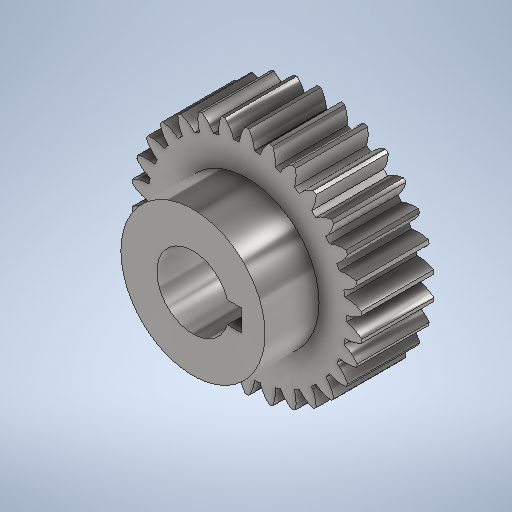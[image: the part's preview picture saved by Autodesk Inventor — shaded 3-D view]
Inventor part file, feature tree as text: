
AUTODESK INVENTOR PART (.ipt)
format: ipt  version: 2025.2 (Build 292293000, 293)  size: 447,488 bytes
history: native  units: in
note: dims shown in document units (in); Inventor stores cm internally (conversion verified against a paired STEP export)
features: sketch x5, extrude x5, fillet x1, pattern_circular x1
ambient origin geometry x8: Origin, YZ Plane, XZ Plane, XY Plane, X Axis, Y Axis, Z Axis, Center Point
bodies: Solid1 (feature_tree)
feature tree (12):
  sketch  "Sketch1"  dims[d0=2.5197in d1=2.3622in]
  extrude  "Extrusion1"  Depth=2.3622in
  extrude  "Extrusion2"  Depth=0.1236in
  fillet  "Fillet1"  Radius=0.0394in
  pattern_circular  "Circular Pattern1"  Count=2  [1 undecoded]
  extrude  "Extrusion3"  Depth=0.0039in
  sketch  "Sketch3"  dims[d5=0.1654in d6=0.7874in d7=0.0in]
  extrude  "Extrusion4"  Depth=0.2362in
  extrude  "Extrusion5"  Depth=0.7874in
  sketch  "Sketch2"  dims[d2=2.1785in d3=0.1236in d4=0.0394in]
  sketch  "Sketch4"  dims[d8=0.7874in d9=0.0in d10=0.0039in]
  sketch  "Sketch5"  dims[d11=11.811in d12=360.0deg d14=1.5748in d15=0.7874in d16=0.5906in d17=0.0in d18=0.7874in d19=0.0in d20=0.0in d21=0.2362in d22=0.5315in d23=0.0in d24=0.0in]
note: 1 required parameter value undecoded (feature->parameter linkage not recoverable at this tier; creation-order binding heuristic only, values carry confidence <= 0.55)
